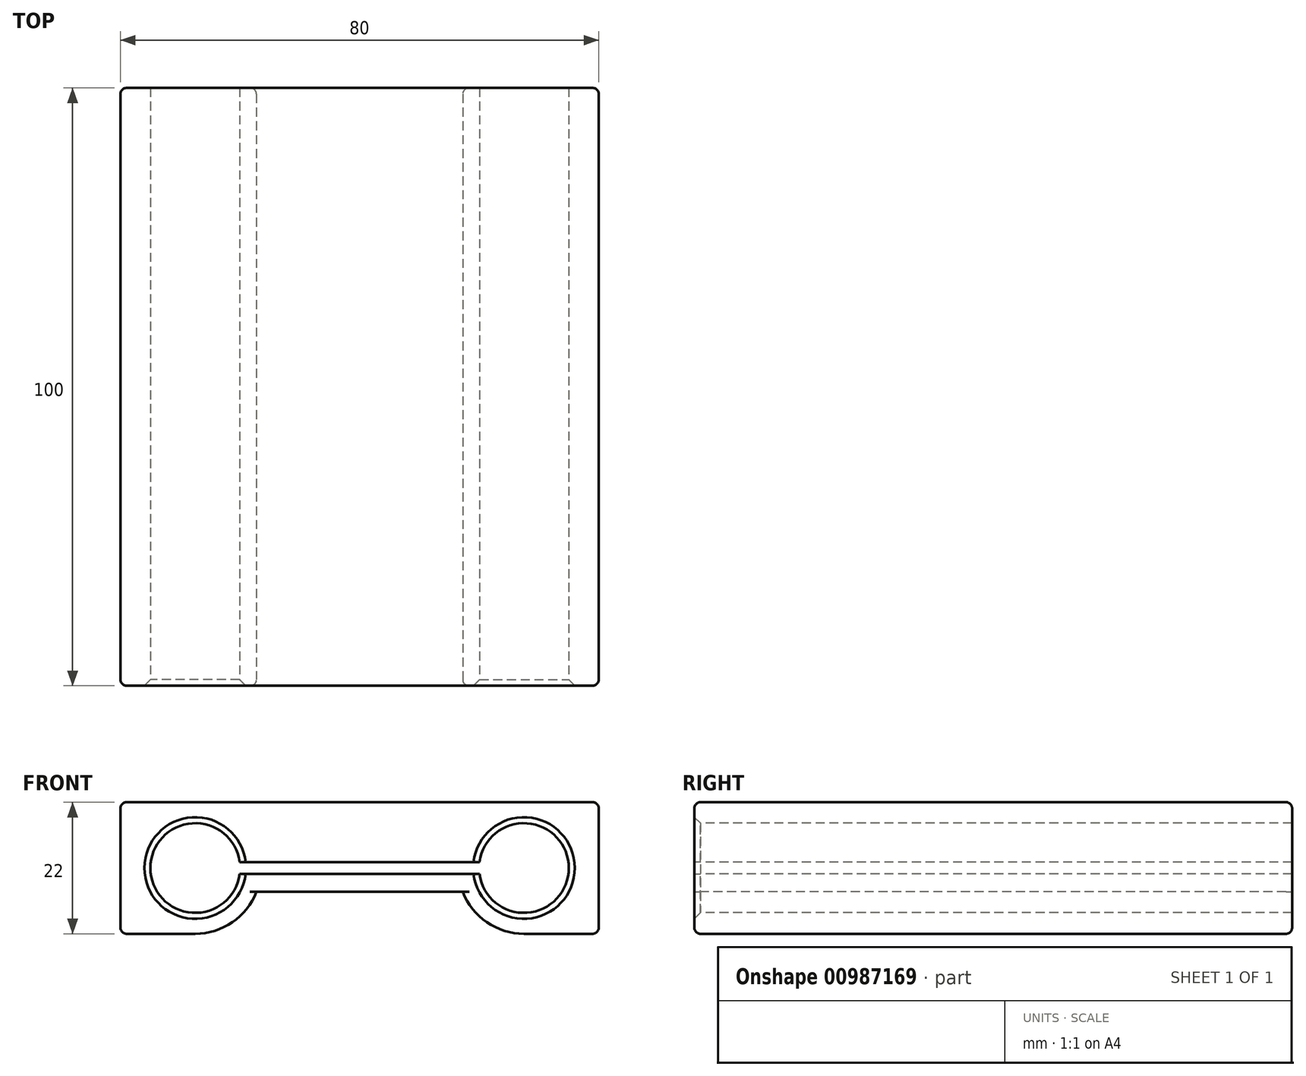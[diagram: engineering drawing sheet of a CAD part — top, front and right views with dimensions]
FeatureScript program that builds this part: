
annotation { "Feature Type Name" : "Feature", "Feature Type Description" : "" }
export const myFeature = defineFeature(function(context is Context, id is Id, definition is map)
    precondition{}
    {
        {
            var Q0;
            Q0=qCreatedBy(makeId("Front.planeOp"),FACE);
            var sketch = newSketch(context, id + "F0", { "sketchPlane" : qUnion([Q0])});
            skLineSegment(sketch, "E0.bottom", {"start": v(-39, 11) * mm, "end": v(39, 11) * mm});
            skLineSegment(sketch, "E0.top", {"start": v(-39, -11) * mm, "end": v(-27.5, -11) * mm});
            skLineSegment(sketch, "E0.left", {"start": v(-40, 10) * mm, "end": v(-40, -10) * mm});
            skLineSegment(sketch, "E0.right", {"start": v(40, 10) * mm, "end": v(40, -10) * mm});
            skPoint(sketch, "E1", {"position": v(0, 0) * mm});
            skPoint(sketch, "E1.positionSnap0", {"position": v(-40, 0) * mm});
            skPoint(sketch, "E1.positionSnap1", {"position": v(0, 11) * mm});
            skArc(sketch, "E2", {"start": v(-20.07, 1) * mm, "mid": v(-35, 0) * mm, "end": v(-20.07, -1) * mm});
            skArc(sketch, "E3", {"start": v(20.07, -1) * mm, "mid": v(35, 0) * mm, "end": v(20.07, 1) * mm});
            skPoint(sketch, "E4.visualSharp", {"position": v(-40, 11) * mm});
            skArc(sketch, "E4.filletArc", {"start": v(-39, 11) * mm, "mid": v(-39.7, 10.7) * mm, "end": v(-40, 10) * mm});
            skPoint(sketch, "E5.visualSharp", {"position": v(-40, -11) * mm});
            skArc(sketch, "E5.filletArc", {"start": v(-40, -10) * mm, "mid": v(-39.7, -10.7) * mm, "end": v(-39, -11) * mm});
            skPoint(sketch, "E6.visualSharp", {"position": v(40, -11) * mm});
            skArc(sketch, "E6.filletArc", {"start": v(39, -11) * mm, "mid": v(39.7, -10.7) * mm, "end": v(40, -10) * mm});
            skPoint(sketch, "E7.visualSharp", {"position": v(40, 11) * mm});
            skLineSegment(sketch, "E8", {"start": v(-40, 0) * mm, "end": v(40, 0) * mm, "construction": true});
            skArc(sketch, "E9", {"start": v(-27.5, -11) * mm, "mid": v(-21.3, -9.08) * mm, "end": v(-17.25, -4) * mm});
            skArc(sketch, "E10", {"start": v(17.25, -4) * mm, "mid": v(21.3, -9.08) * mm, "end": v(27.5, -11) * mm});
            skLineSegment(sketch, "E11", {"start": v(-20.07, 1) * mm, "end": v(20.07, 1) * mm});
            skLineSegment(sketch, "E12", {"start": v(-17.25, -4) * mm, "end": v(17.25, -4) * mm});
            skLineSegment(sketch, "E13.trimOffspring", {"start": v(27.5, -11) * mm, "end": v(39, -11) * mm});
            skLineSegment(sketch, "E14", {"start": v(-20.07, -1) * mm, "end": v(20.07, -1) * mm});
            skArc(sketch, "E15", {"start": v(39, 11) * mm, "mid": v(39.7, 10.7) * mm, "end": v(40, 10) * mm});
            skSolve(sketch);
        }
        {
            var Q0;
            Q0=makeQuery(id+"F0.imprint","IMPRINT",FACE,{"disambiguationData":[TD([[makeQuery(id+"F0.imprint","IMPRINT",EDGE,{"derivedFrom":sQuery(id+"F0.wireOp",EDGE,"E0.bottom")}),-1.0]])]});
            extrude(context, id + "F1", {"entities" : qUnion([Q0]), "oppositeDirection" : true, "depth" : 100 * mm, "offsetDistance" : 25 * mm});
        }
        {
            var Q0;
            Q0=makeQuery(id+"F1.opExtrude","SWEPT_FACE",FACE,{"disambiguationData":[OSD([sQuery(id+"F0.wireOp",EDGE,"E0.bottom")])]});
            fillet(context, id + "F2", {"entities" : qUnion([Q0]), "radius" : 1 * mm, "tangentPropagation" : true, "allowEdgeOverflow" : false});
        }
        {
            var Q0;
            Q0=makeQuery(id+"F1.opExtrude","CAP_EDGE",EDGE,{"disambiguationData":[OSD([sQuery(id+"F0.wireOp",EDGE,"E2")])],"isStart":true});
            var Q1;
            Q1=makeQuery(id+"F1.opExtrude","CAP_EDGE",EDGE,{"disambiguationData":[OSD([sQuery(id+"F0.wireOp",EDGE,"E3")])],"isStart":true});
            chamfer(context, id + "F3", {"entities" : qUnion([Q0, Q1]), "width" : 1 * mm, "tangentPropagation" : true});
        }
    });
